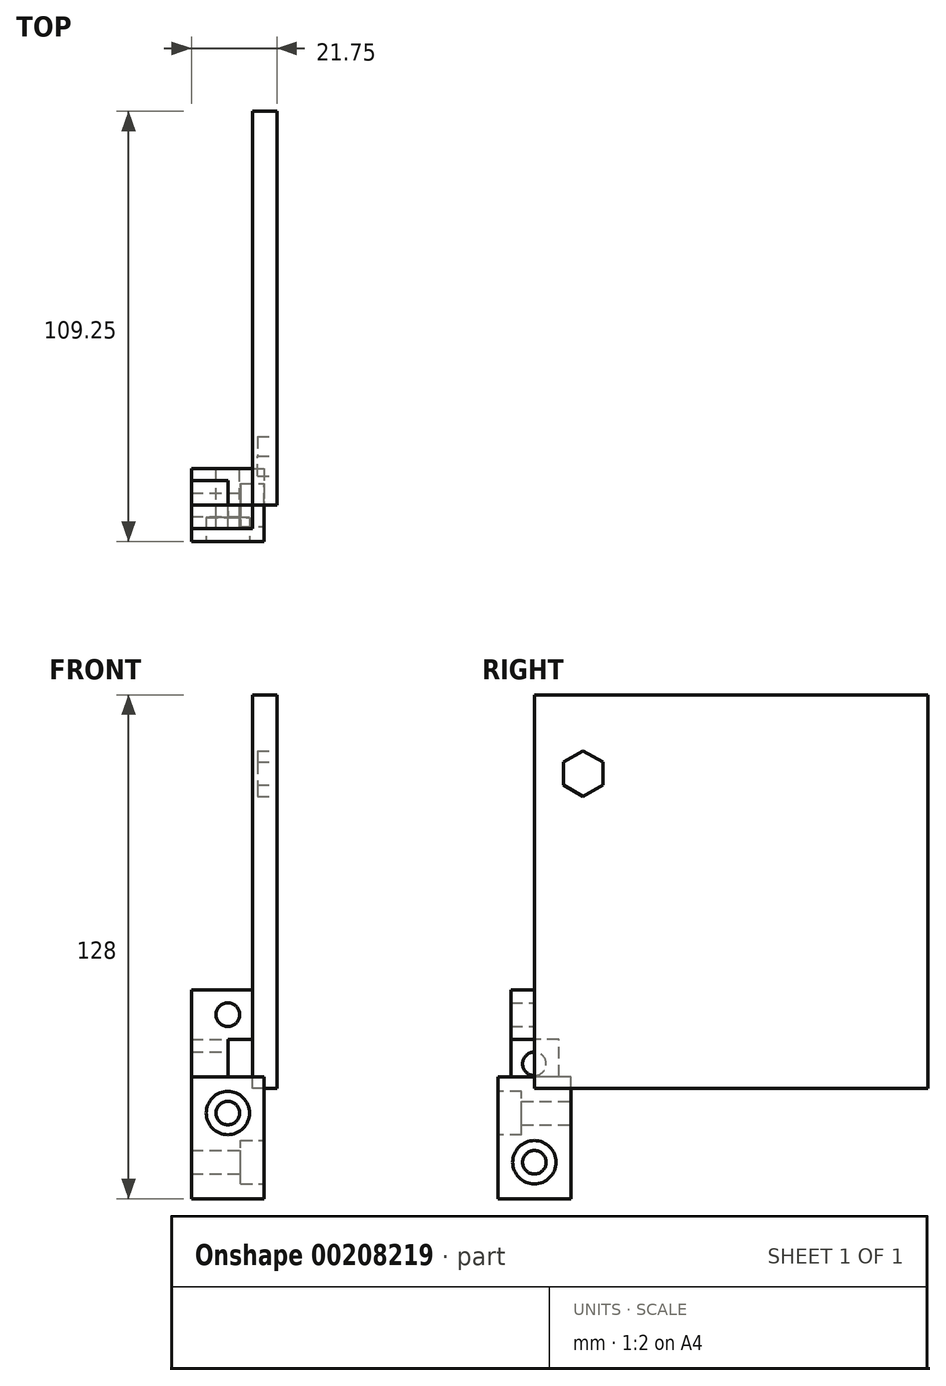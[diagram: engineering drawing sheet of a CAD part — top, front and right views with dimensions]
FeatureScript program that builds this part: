
annotation { "Feature Type Name" : "Feature", "Feature Type Description" : "" }
export const myFeature = defineFeature(function(context is Context, id is Id, definition is map)
    precondition{}
    {
        {
            var Q0;
            Q0=qCreatedBy(makeId("Front.planeOp"),FACE);
            var sketch = newSketch(context, id + "F0", { "sketchPlane" : qUnion([Q0])});
            skLineSegment(sketch, "E0.bottom", {"start": v(-12.5, 25) * mm, "end": v(0, 25) * mm});
            skLineSegment(sketch, "E0.top", {"start": v(-12.5, 0) * mm, "end": v(0, 0) * mm});
            skLineSegment(sketch, "E0.left", {"start": v(-12.5, 25) * mm, "end": v(-12.5, 0) * mm});
            skLineSegment(sketch, "E0.right", {"start": v(0, 25) * mm, "end": v(0, 0) * mm});
            skCircle(sketch, "E1", {"center": v(-6.25, 18.75) * mm, "radius": 3 * mm});
            skLineSegment(sketch, "E2", {"start": v(-6.25, 25) * mm, "end": v(-6.25, 12.5) * mm, "construction": true});
            skPoint(sketch, "E2.endSnap0", {"position": v(-12.5, 12.5) * mm});
            skSolve(sketch);
        }
        {
            var Q0;
            Q0=makeQuery(id+"F0.imprint","IMPRINT",FACE,{"disambiguationData":[TD([[makeQuery(id+"F0.imprint","IMPRINT",EDGE,{"derivedFrom":sQuery(id+"F0.wireOp",EDGE,"E0.bottom")}),-1.0]])]});
            extrude(context, id + "F1", {"entities" : qUnion([Q0]), "depth" : 6 * mm});
        }
        {
            var Q0;
            Q0=qCreatedBy(makeId("Right.planeOp"),FACE);
            var sketch = newSketch(context, id + "F2", { "sketchPlane" : qUnion([Q0])});
            skLineSegment(sketch, "E3.bottom", {"start": v(6.25, 0) * mm, "end": v(0, 0) * mm});
            skLineSegment(sketch, "E3.top", {"start": v(6.25, 12.5) * mm, "end": v(0, 12.5) * mm});
            skLineSegment(sketch, "E3.left", {"start": v(6.25, 0) * mm, "end": v(6.25, 12.5) * mm});
            skLineSegment(sketch, "E3.right", {"start": v(0, 0) * mm, "end": v(0, 12.5) * mm});
            skSolve(sketch);
        }
        {
            var Q0;
            Q0=makeQuery(id+"F2.imprint","IMPRINT",FACE,{"disambiguationData":[TD([[makeQuery(id+"F2.imprint","IMPRINT",EDGE,{"derivedFrom":sQuery(id+"F2.wireOp",EDGE,"E3.bottom")}),-1.0]])]});
            extrude(context, id + "F3", {"entities" : qUnion([Q0]), "operationType" : NewBodyOperationType.ADD, "oppositeDirection" : true, "depth" : 12.5 * mm, "hasSecondDirection" : true, "secondDirectionOppositeDirection" : true, "secondDirectionDepth" : 6.25 * mm});
        }
        {
            var Q0;
            Q0=makeQuery(id+"F1.opExtrude","CAP_FACE",FACE,{"disambiguationData":[OSD([sQuery(id+"F0.wireOp",EDGE,"E0.bottom"),sQuery(id+"F0.wireOp",EDGE,"E0.top"),sQuery(id+"F0.wireOp",EDGE,"E0.left"),sQuery(id+"F0.wireOp",EDGE,"E0.right"),sQuery(id+"F0.wireOp",EDGE,"E1")])],"isStart":true});
            var sketch = newSketch(context, id + "F4", { "sketchPlane" : qUnion([Q0])});
            skLineSegment(sketch, "E4.bottom", {"start": v(6.25, 12.5) * mm, "end": v(0, 12.5) * mm});
            skLineSegment(sketch, "E4.top", {"start": v(6.25, 0) * mm, "end": v(0, 0) * mm});
            skLineSegment(sketch, "E4.left", {"start": v(6.25, 12.5) * mm, "end": v(6.25, 0) * mm});
            skLineSegment(sketch, "E4.right", {"start": v(0, 12.5) * mm, "end": v(0, 0) * mm});
            skSolve(sketch);
        }
        {
            var Q0;
            Q0 = qSketchRegion(id + "F4", true);
            extrude(context, id + "F5", {"entities" : qUnion([Q0]), "operationType" : NewBodyOperationType.REMOVE, "oppositeDirection" : true, "depth" : 25 * mm});
        }
        {
            var Q0;
            Q0=makeQuery(id+"F5.boolean.opBoolean","MERGE",FACE,{"derivedFrom":[makeQuery(id+"F3.opExtrude","CAP_FACE",FACE,{"disambiguationData":[OSD([sQuery(id+"F2.wireOp",EDGE,"E3.bottom"),sQuery(id+"F2.wireOp",EDGE,"E3.top"),sQuery(id+"F2.wireOp",EDGE,"E3.left"),sQuery(id+"F2.wireOp",EDGE,"E3.right")])],"isStart":true}),makeQuery(id+"F5.opExtrude","SWEPT_FACE",FACE,{"disambiguationData":[OSD([sQuery(id+"F4.wireOp",EDGE,"E4.left")])]})]});
            var sketch = newSketch(context, id + "F6", { "sketchPlane" : qUnion([Q0])});
            skCircle(sketch, "E5", {"center": v(0, 6.25) * mm, "radius": 3 * mm});
            skLineSegment(sketch, "E6", {"start": v(0, 6.25) * mm, "end": v(0, 0) * mm, "construction": true});
            skSolve(sketch);
        }
        {
            var Q0;
            Q0=makeQuery(id+"F6.imprint","IMPRINT",FACE,{"disambiguationData":[TD([[makeQuery(id+"F6.imprint","IMPRINT",EDGE,{"derivedFrom":sQuery(id+"F6.wireOp",EDGE,"E5")}),1.0]])]});
            extrude(context, id + "F7", {"entities" : qUnion([Q0]), "operationType" : NewBodyOperationType.REMOVE, "oppositeDirection" : true, "depth" : 25 * mm});
        }
        {
            var Q0;
            Q0=qCreatedBy(makeId("Front.planeOp"),FACE);
            var sketch = newSketch(context, id + "F8", { "sketchPlane" : qUnion([Q0])});
            skLineSegment(sketch, "E7.bottom", {"start": v(-12.5, -25) * mm, "end": v(0, -25) * mm});
            skLineSegment(sketch, "E7.top", {"start": v(-12.5, 0) * mm, "end": v(0, 0) * mm});
            skLineSegment(sketch, "E7.left", {"start": v(-12.5, -25) * mm, "end": v(-12.5, 0) * mm});
            skLineSegment(sketch, "E7.right", {"start": v(0, -25) * mm, "end": v(0, 0) * mm});
            skSolve(sketch);
        }
        {
            var Q0;
            Q0 = qSketchRegion(id + "F8", true);
            extrude(context, id + "F9", {"entities" : qUnion([Q0]), "oppositeDirection" : true, "depth" : 6.25 * mm, "hasSecondDirection" : true, "secondDirectionOppositeDirection" : false, "secondDirectionDepth" : 6.25 * mm});
        }
        {
            var Q0;
            Q0=makeQuery(id+"F9.opExtrude","CAP_FACE",FACE,{"disambiguationData":[OSD([sQuery(id+"F8.wireOp",EDGE,"E7.bottom"),sQuery(id+"F8.wireOp",EDGE,"E7.top"),sQuery(id+"F8.wireOp",EDGE,"E7.left"),sQuery(id+"F8.wireOp",EDGE,"E7.right")])],"isStart":false});
            var sketch = newSketch(context, id + "F10", { "sketchPlane" : qUnion([Q0])});
            skCircle(sketch, "E8", {"center": v(6.25, -6.25) * mm, "radius": 3 * mm});
            skLineSegment(sketch, "E9", {"start": v(6.25, 0) * mm, "end": v(6.25, -6.25) * mm, "construction": true});
            skSolve(sketch);
        }
        {
            var Q0;
            Q0 = qSketchRegion(id + "F10", true);
            var Q1;
            Q1=sQuery(id+"F10.wireOp",EDGE,"E8");
            extrude(context, id + "F11", {"entities" : qUnion([Q0]), "operationType" : NewBodyOperationType.REMOVE, "surfaceEntities" : qUnion([Q1]), "oppositeDirection" : true, "depth" : 25 * mm});
        }
        {
            var Q0;
            Q0=makeQuery(id+"F9.opExtrude","SWEPT_FACE",FACE,{"disambiguationData":[OSD([sQuery(id+"F8.wireOp",EDGE,"E7.right")])]});
            var sketch = newSketch(context, id + "F12", { "sketchPlane" : qUnion([Q0])});
            skLineSegment(sketch, "E10", {"start": v(0, -25) * mm, "end": v(0, -18.75) * mm, "construction": true});
            skCircle(sketch, "E11", {"center": v(0, -18.75) * mm, "radius": 3 * mm});
            skSolve(sketch);
        }
        {
            var Q0;
            Q0 = qSketchRegion(id + "F12", true);
            extrude(context, id + "F13", {"entities" : qUnion([Q0]), "operationType" : NewBodyOperationType.REMOVE, "oppositeDirection" : true, "depth" : 25 * mm});
        }
        {
            var Q0;
            Q0=makeQuery(id+"F9.opExtrude","CAP_FACE",FACE,{"disambiguationData":[OSD([sQuery(id+"F8.wireOp",EDGE,"E7.bottom"),sQuery(id+"F8.wireOp",EDGE,"E7.top"),sQuery(id+"F8.wireOp",EDGE,"E7.left"),sQuery(id+"F8.wireOp",EDGE,"E7.right")])],"isStart":true});
            extrude(context, id + "F14", {"entities" : qUnion([Q0]), "operationType" : NewBodyOperationType.ADD, "depth" : 3 * mm});
        }
        {
            var Q0;
            Q0=makeQuery(id+"F9.opExtrude","CAP_FACE",FACE,{"disambiguationData":[OSD([sQuery(id+"F8.wireOp",EDGE,"E7.bottom"),sQuery(id+"F8.wireOp",EDGE,"E7.top"),sQuery(id+"F8.wireOp",EDGE,"E7.left"),sQuery(id+"F8.wireOp",EDGE,"E7.right")])],"isStart":false});
            extrude(context, id + "F15", {"entities" : qUnion([Q0]), "operationType" : NewBodyOperationType.ADD, "depth" : 3 * mm});
        }
        {
            var Q0;
            {var subQ0=sQuery(id+"F8.wireOp",EDGE,"E7.right");Q0=makeQuery(id+"F15.boolean.opBoolean","MERGE",FACE,{"derivedFrom":[makeQuery(id+"F14.boolean.opBoolean","MERGE",FACE,{"derivedFrom":[makeQuery(id+"F9.opExtrude","SWEPT_FACE",FACE,{"disambiguationData":[OSD([subQ0])]}),makeQuery(id+"F14.opExtrude","SWEPT_FACE",FACE,{"disambiguationData":[OSD([subQ0])]})]}),makeQuery(id+"F15.opExtrude","SWEPT_FACE",FACE,{"disambiguationData":[OSD([subQ0])]})]});}
            extrude(context, id + "F16", {"entities" : qUnion([Q0]), "operationType" : NewBodyOperationType.ADD, "depth" : 3 * mm});
        }
        {
            var Q0;
            {var subQ0=sQuery(id+"F8.wireOp",EDGE,"E7.left");Q0=makeQuery(id+"F15.boolean.opBoolean","MERGE",FACE,{"derivedFrom":[makeQuery(id+"F14.boolean.opBoolean","MERGE",FACE,{"derivedFrom":[makeQuery(id+"F9.opExtrude","SWEPT_FACE",FACE,{"disambiguationData":[OSD([subQ0])]}),makeQuery(id+"F14.opExtrude","SWEPT_FACE",FACE,{"disambiguationData":[OSD([subQ0])]})]}),makeQuery(id+"F15.opExtrude","SWEPT_FACE",FACE,{"disambiguationData":[OSD([subQ0])]})]});}
            extrude(context, id + "F17", {"entities" : qUnion([Q0]), "operationType" : NewBodyOperationType.ADD, "depth" : 3 * mm});
        }
        {
            var Q0;
            {var subQ0=sQuery(id+"F8.wireOp",EDGE,"E7.top");Q0=makeQuery(id+"F17.boolean.opBoolean","MERGE",FACE,{"derivedFrom":[makeQuery(id+"F16.boolean.opBoolean","MERGE",FACE,{"derivedFrom":[makeQuery(id+"F15.boolean.opBoolean","MERGE",FACE,{"derivedFrom":[makeQuery(id+"F14.boolean.opBoolean","MERGE",FACE,{"derivedFrom":[makeQuery(id+"F9.opExtrude","SWEPT_FACE",FACE,{"disambiguationData":[OSD([subQ0])]}),makeQuery(id+"F14.opExtrude","SWEPT_FACE",FACE,{"disambiguationData":[OSD([subQ0])]})]}),makeQuery(id+"F15.opExtrude","SWEPT_FACE",FACE,{"disambiguationData":[OSD([subQ0])]})]}),makeQuery(id+"F16.opExtrude","SWEPT_FACE",FACE,{"disambiguationData":[OSD([subQ0,sQuery(id+"F8.wireOp",EDGE,"E7.right")])]})]}),makeQuery(id+"F17.opExtrude","SWEPT_FACE",FACE,{"disambiguationData":[OSD([subQ0,sQuery(id+"F8.wireOp",EDGE,"E7.left")])]})]});}
            extrude(context, id + "F18", {"entities" : qUnion([Q0]), "operationType" : NewBodyOperationType.ADD, "depth" : 3 * mm});
        }
        {
            var Q0;
            {var subQ0=sQuery(id+"F8.wireOp",EDGE,"E7.bottom");Q0=makeQuery(id+"F17.boolean.opBoolean","MERGE",FACE,{"derivedFrom":[makeQuery(id+"F16.boolean.opBoolean","MERGE",FACE,{"derivedFrom":[makeQuery(id+"F15.boolean.opBoolean","MERGE",FACE,{"derivedFrom":[makeQuery(id+"F14.boolean.opBoolean","MERGE",FACE,{"derivedFrom":[makeQuery(id+"F9.opExtrude","SWEPT_FACE",FACE,{"disambiguationData":[OSD([subQ0])]}),makeQuery(id+"F14.opExtrude","SWEPT_FACE",FACE,{"disambiguationData":[OSD([subQ0])]})]}),makeQuery(id+"F15.opExtrude","SWEPT_FACE",FACE,{"disambiguationData":[OSD([subQ0])]})]}),makeQuery(id+"F16.opExtrude","SWEPT_FACE",FACE,{"disambiguationData":[OSD([subQ0,sQuery(id+"F8.wireOp",EDGE,"E7.right")])]})]}),makeQuery(id+"F17.opExtrude","SWEPT_FACE",FACE,{"disambiguationData":[OSD([subQ0,sQuery(id+"F8.wireOp",EDGE,"E7.left")])]})]});}
            extrude(context, id + "F19", {"entities" : qUnion([Q0]), "operationType" : NewBodyOperationType.ADD, "depth" : 3 * mm});
        }
        {
            var Q0;
            {var subQ0=sQuery(id+"F8.wireOp",EDGE,"E7.right");Q0=makeQuery(id+"F19.boolean.opBoolean","MERGE",FACE,{"derivedFrom":[makeQuery(id+"F18.boolean.opBoolean","MERGE",FACE,{"derivedFrom":[makeQuery(id+"F16.opExtrude","CAP_FACE",FACE,{"disambiguationData":[OSD([subQ0])],"isStart":false}),makeQuery(id+"F18.opExtrude","SWEPT_FACE",FACE,{"disambiguationData":[OSD([sQuery(id+"F8.wireOp",EDGE,"E7.top"),subQ0])]})]}),makeQuery(id+"F19.opExtrude","SWEPT_FACE",FACE,{"disambiguationData":[OSD([sQuery(id+"F8.wireOp",EDGE,"E7.bottom"),subQ0])]})]});}
            var sketch = newSketch(context, id + "F20", { "sketchPlane" : qUnion([Q0])});
            skCircle(sketch, "E12", {"center": v(0, -18.75) * mm, "radius": 5.5 * mm});
            skSolve(sketch);
        }
        {
            var Q0;
            Q0=makeQuery(id+"F20.imprint","IMPRINT",FACE,{"disambiguationData":[TD([[makeQuery(id+"F20.imprint","IMPRINT",EDGE,{"derivedFrom":sQuery(id+"F20.wireOp",EDGE,"E12")}),1.0]])]});
            var Q1;
            Q1=sQuery(id+"F20.wireOp",EDGE,"E12");
            extrude(context, id + "F21", {"entities" : qUnion([Q0]), "operationType" : NewBodyOperationType.REMOVE, "surfaceEntities" : qUnion([Q1]), "oppositeDirection" : true, "depth" : 6 * mm});
        }
        {
            var Q0;
            {var subQ0=sQuery(id+"F8.wireOp",EDGE,"E7.left");var subQ1=sQuery(id+"F8.wireOp",EDGE,"E7.bottom");var subQ2=sQuery(id+"F8.wireOp",EDGE,"E7.right");var subQ3=sQuery(id+"F8.wireOp",EDGE,"E7.top");Q0=makeQuery(id+"F19.boolean.opBoolean","MERGE",FACE,{"derivedFrom":[makeQuery(id+"F18.boolean.opBoolean","MERGE",FACE,{"derivedFrom":[makeQuery(id+"F17.boolean.opBoolean","MERGE",FACE,{"derivedFrom":[makeQuery(id+"F16.boolean.opBoolean","MERGE",FACE,{"derivedFrom":[makeQuery(id+"F14.opExtrude","CAP_FACE",FACE,{"disambiguationData":[OSD([subQ1,subQ3,subQ0,subQ2])],"isStart":false}),makeQuery(id+"F16.opExtrude","SWEPT_FACE",FACE,{"disambiguationData":[OSD([subQ2]),TDD([makeQuery(id+"F14.opExtrude","CAP_EDGE",EDGE,{"disambiguationData":[OSD([subQ2])],"isStart":false})])]})]}),makeQuery(id+"F17.opExtrude","SWEPT_FACE",FACE,{"disambiguationData":[OSD([subQ0]),TDD([makeQuery(id+"F14.opExtrude","CAP_EDGE",EDGE,{"disambiguationData":[OSD([subQ0])],"isStart":false})])]})]}),makeQuery(id+"F18.opExtrude","SWEPT_FACE",FACE,{"disambiguationData":[OSD([subQ3,subQ0,subQ2]),TDD([makeQuery(id+"F17.boolean.opBoolean","MERGE",EDGE,{"derivedFrom":[makeQuery(id+"F16.boolean.opBoolean","MERGE",EDGE,{"derivedFrom":[makeQuery(id+"F14.opExtrude","CAP_EDGE",EDGE,{"disambiguationData":[OSD([subQ3])],"isStart":false}),makeQuery(id+"F16.opExtrude","SWEPT_EDGE",EDGE,{"disambiguationData":[OSD([subQ3,subQ2]),TDD([makeQuery(id+"F14.opExtrude","CAP_VERTEX",VERTEX,{"disambiguationData":[OSD([subQ3,subQ2])],"isStart":false})])]})]}),makeQuery(id+"F17.opExtrude","SWEPT_EDGE",EDGE,{"disambiguationData":[OSD([subQ3,subQ0]),TDD([makeQuery(id+"F14.opExtrude","CAP_VERTEX",VERTEX,{"disambiguationData":[OSD([subQ3,subQ0])],"isStart":false})])]})]})])]})]}),makeQuery(id+"F19.opExtrude","SWEPT_FACE",FACE,{"disambiguationData":[OSD([subQ1,subQ0,subQ2]),TDD([makeQuery(id+"F17.boolean.opBoolean","MERGE",EDGE,{"derivedFrom":[makeQuery(id+"F16.boolean.opBoolean","MERGE",EDGE,{"derivedFrom":[makeQuery(id+"F14.opExtrude","CAP_EDGE",EDGE,{"disambiguationData":[OSD([subQ1])],"isStart":false}),makeQuery(id+"F16.opExtrude","SWEPT_EDGE",EDGE,{"disambiguationData":[OSD([subQ1,subQ2]),TDD([makeQuery(id+"F14.opExtrude","CAP_VERTEX",VERTEX,{"disambiguationData":[OSD([subQ1,subQ2])],"isStart":false})])]})]}),makeQuery(id+"F17.opExtrude","SWEPT_EDGE",EDGE,{"disambiguationData":[OSD([subQ1,subQ0]),TDD([makeQuery(id+"F14.opExtrude","CAP_VERTEX",VERTEX,{"disambiguationData":[OSD([subQ1,subQ0])],"isStart":false})])]})]})])]})]});}
            var sketch = newSketch(context, id + "F22", { "sketchPlane" : qUnion([Q0])});
            skCircle(sketch, "E13", {"center": v(-6.25, -6.25) * mm, "radius": 5.5 * mm});
            skSolve(sketch);
        }
        {
            var Q0;
            Q0=makeQuery(id+"F22.imprint","IMPRINT",FACE,{"disambiguationData":[TD([[makeQuery(id+"F22.imprint","IMPRINT",EDGE,{"derivedFrom":sQuery(id+"F22.wireOp",EDGE,"E13")}),1.0]])]});
            extrude(context, id + "F23", {"entities" : qUnion([Q0]), "operationType" : NewBodyOperationType.REMOVE, "oppositeDirection" : true, "depth" : 6 * mm});
        }
        {
            var Q0;
            Q0=qCreatedBy(makeId("Right.planeOp"),FACE);
            var sketch = newSketch(context, id + "F24", { "sketchPlane" : qUnion([Q0])});
            skLineSegment(sketch, "E14.bottom", {"start": v(100, 0) * mm, "end": v(0, 0) * mm});
            skLineSegment(sketch, "E14.top", {"start": v(100, 100) * mm, "end": v(0, 100) * mm});
            skLineSegment(sketch, "E14.left", {"start": v(100, 0) * mm, "end": v(100, 100) * mm});
            skLineSegment(sketch, "E14.right", {"start": v(0, 0) * mm, "end": v(0, 100) * mm});
            skSolve(sketch);
        }
        {
            var Q0;
            Q0=makeQuery(id+"F24.imprint","IMPRINT",FACE,{"disambiguationData":[TD([[makeQuery(id+"F24.imprint","IMPRINT",EDGE,{"derivedFrom":sQuery(id+"F24.wireOp",EDGE,"E14.bottom")}),-1.0]])]});
            extrude(context, id + "F25", {"entities" : qUnion([Q0]), "depth" : 6.25 * mm});
        }
        {
            var Q0;
            Q0=makeQuery(id+"F25.opExtrude","CAP_FACE",FACE,{"disambiguationData":[OSD([sQuery(id+"F24.wireOp",EDGE,"E14.bottom"),sQuery(id+"F24.wireOp",EDGE,"E14.top"),sQuery(id+"F24.wireOp",EDGE,"E14.left"),sQuery(id+"F24.wireOp",EDGE,"E14.right")])],"isStart":false});
            var sketch = newSketch(context, id + "F26", { "sketchPlane" : qUnion([Q0])});
            skCircle(sketch, "E15.cCircle", {"center": v(12.37, 80) * mm, "radius": 5 * mm, "construction": true});
            skLineSegment(sketch, "E15.0", {"start": v(17.37, 77.11) * mm, "end": v(12.37, 74.23) * mm});
            skLineSegment(sketch, "E15.1", {"start": v(12.37, 74.23) * mm, "end": v(7.37, 77.11) * mm});
            skLineSegment(sketch, "E15.2", {"start": v(7.37, 77.11) * mm, "end": v(7.37, 82.89) * mm});
            skLineSegment(sketch, "E15.3", {"start": v(7.38, 82.89) * mm, "end": v(12.38, 85.77) * mm});
            skLineSegment(sketch, "E15.4", {"start": v(12.37, 85.77) * mm, "end": v(17.37, 82.89) * mm});
            skLineSegment(sketch, "E15.5", {"start": v(17.37, 82.89) * mm, "end": v(17.37, 77.11) * mm});
            skPoint(sketch, "E15.0.midPoint", {"position": v(14.87, 75.67) * mm});
            skLineSegment(sketch, "E16", {"start": v(3.12, 100) * mm, "end": v(3.13, 0) * mm, "construction": true});
            skSolve(sketch);
        }
        {
            var Q0;
            Q0 = qSketchRegion(id + "F26", true);
            extrude(context, id + "F27", {"entities" : qUnion([Q0]), "operationType" : NewBodyOperationType.REMOVE, "oppositeDirection" : true, "depth" : 5 * mm});
        }
    });
